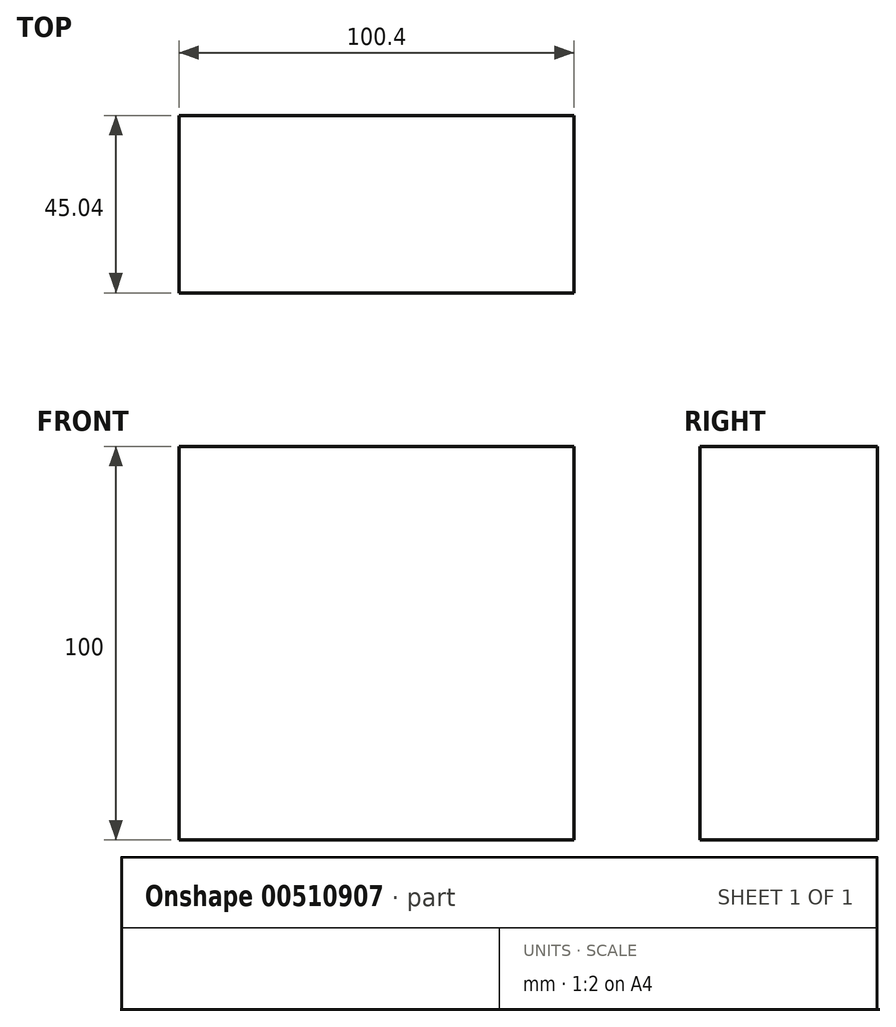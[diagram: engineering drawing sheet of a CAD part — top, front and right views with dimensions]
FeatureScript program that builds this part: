
annotation { "Feature Type Name" : "Feature", "Feature Type Description" : "" }
export const myFeature = defineFeature(function(context is Context, id is Id, definition is map)
    precondition{}
    {
        {
            var Q0;
            Q0=qCreatedBy(makeId("Top.planeOp"),FACE);
            var sketch = newSketch(context, id + "F0", { "sketchPlane" : qUnion([Q0])});
            skLineSegment(sketch, "E0.bottom", {"start": v(-50.2, -22.52) * mm, "end": v(50.2, -22.52) * mm});
            skLineSegment(sketch, "E0.top", {"start": v(-50.2, 22.52) * mm, "end": v(50.2, 22.52) * mm});
            skLineSegment(sketch, "E0.left", {"start": v(-50.2, -22.52) * mm, "end": v(-50.2, 22.52) * mm});
            skLineSegment(sketch, "E0.right", {"start": v(50.2, -22.52) * mm, "end": v(50.2, 22.52) * mm});
            skPoint(sketch, "E0.middle", {"position": v(0, 0) * mm});
            skSolve(sketch);
        }
        {
            var Q0;
            Q0 = qSketchRegion(id + "F0", true);
            extrude(context, id + "F1", {"entities" : qUnion([Q0]), "depth" : 100 * mm});
        }
    });
